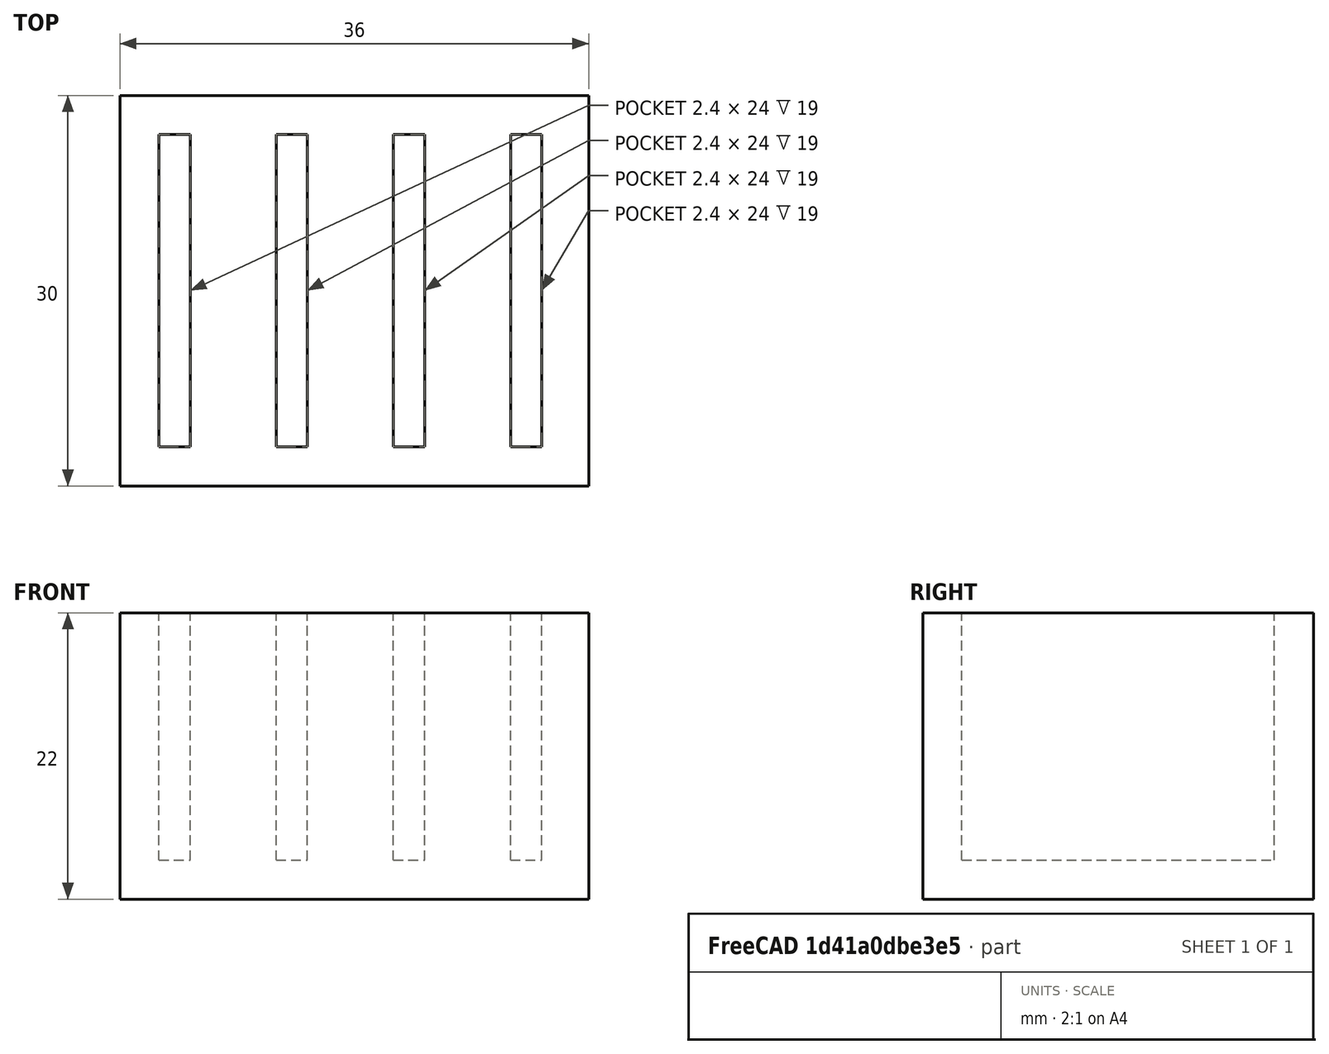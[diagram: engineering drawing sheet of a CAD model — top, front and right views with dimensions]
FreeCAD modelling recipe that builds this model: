
FCSTD DOCUMENT  (FreeCAD 0.21R33694 (Git))
Label: OJT1_T08R01_partacartes
License: All rights reserved
LicenseURL: http://en.wikipedia.org/wiki/All_rights_reserved
objects: Part::Box×5, Part::MultiFuse×1, Part::Cut×1
note: 7 computed .brp shape members not serialized (recipe doc carries the construction recipe); baked Part::Feature solids carry a one-line shape summary decoded from their .brp

FEATURE [Part::Box] Box  label="Ranura 1"
  AttacherType = Attacher::AttachEngine3D
  Height = 22
  Length = 2.4
  Width = 24
FEATURE [Part::Box] Box001  label="Ranura 2"
  AttacherType = Attacher::AttachEngine3D
  Height = 22
  Length = 2.4
  Placement = pos=(9,0,0) rot=(0,0,1;0rad)
  Width = 24
FEATURE [Part::Box] Box002  label="Ranura 3"
  AttacherType = Attacher::AttachEngine3D
  Height = 22
  Length = 2.4
  Placement = pos=(18,0,0) rot=(0,0,1;0rad)
  Width = 24
FEATURE [Part::Box] Box003  label="Ranura 4"
  AttacherType = Attacher::AttachEngine3D
  Height = 22
  Length = 2.4
  Placement = pos=(27,0,0) rot=(0,0,1;0rad)
  Width = 24
FEATURE [Part::MultiFuse] Fusion  label="Ranuras"
  Placement = pos=(0,0,3) rot=(0,0,1;0rad)
  Refine = true
  Shapes = -> [Box003,Box,Box001,Box002]
FEATURE [Part::Box] Box004  label="Base"
  AttacherType = Attacher::AttachEngine3D
  Height = 22
  Length = 36
  Placement = pos=(-3,-3,0) rot=(0,0,1;0rad)
  Width = 30
FEATURE [Part::Cut] Cut
  Base = -> Box004
  Refine = true
  Tool = -> Fusion
